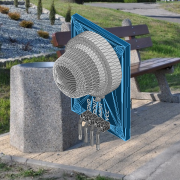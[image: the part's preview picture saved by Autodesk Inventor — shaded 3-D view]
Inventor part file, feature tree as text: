
AUTODESK INVENTOR PART (.ipt)
format: ipt  version: 2021 (Build 250183000, 183)  size: 327,168 bytes
history: native  units: mm
features: extrude x1, sketch x1, other x1
ambient origin geometry x8: Origin, YZ Plane, XZ Plane, XY Plane, X Axis, Y Axis, Z Axis, Center Point
bodies: Solid1 (feature_tree)
feature tree (3):
  extrude  "Extrusion1"  [1 undecoded]
  sketch  "Sketch1"  dims[d0=0.2mm d1=0.0mm]
  other  "MeshFeature1"
note: 1 required parameter value undecoded (feature->parameter linkage not recoverable at this tier; creation-order binding heuristic only, values carry confidence <= 0.55)
